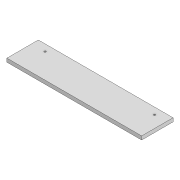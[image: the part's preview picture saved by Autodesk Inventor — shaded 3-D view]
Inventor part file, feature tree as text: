
AUTODESK INVENTOR PART (.ipt)
format: ipt  version: 2022 (Build 260153000, 153)  size: 83,456 bytes
history: native  units: mm
features: extrude x1, sketch x1
ambient origin geometry x8: Origin, YZ Plane, XZ Plane, XY Plane, X Axis, Y Axis, Z Axis, Center Point
bodies: Solid1 (feature_tree)
feature tree (2):
  extrude  "Extrusion1"  Depth=70.0mm
  sketch  "Sketch1"  dims[d0=300.0mm d1=70.0mm d2=4.0mm d3=4.0mm d4=243.651mm d5=30.0mm d6=15.0mm d7=15.0mm d8=8.0mm d9=0.0mm]
